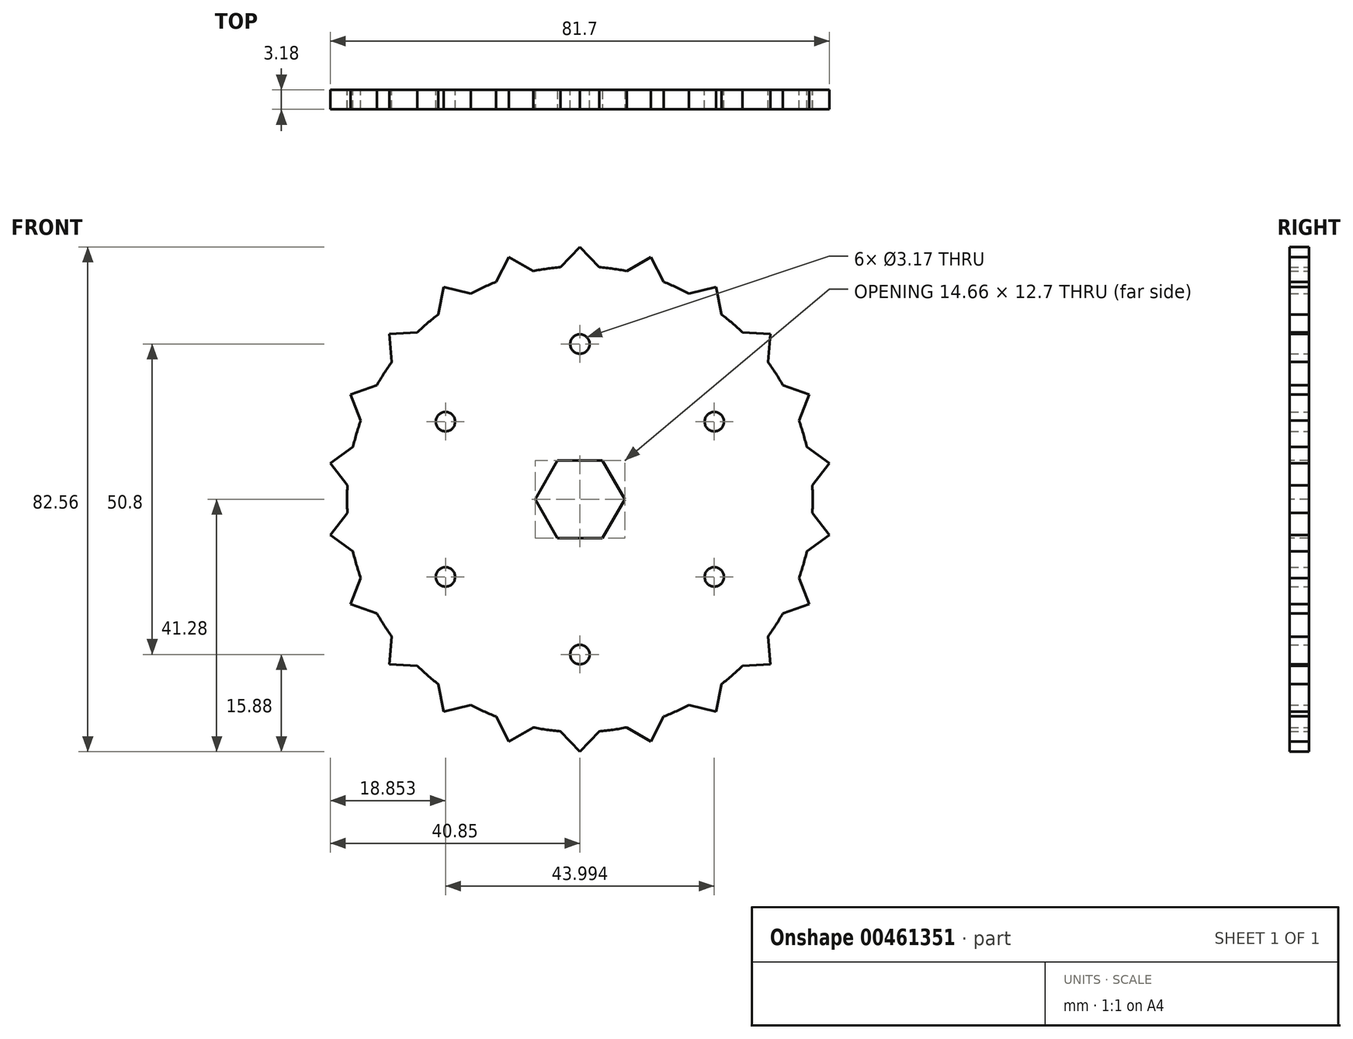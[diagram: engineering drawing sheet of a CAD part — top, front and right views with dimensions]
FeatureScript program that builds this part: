
annotation { "Feature Type Name" : "Feature", "Feature Type Description" : "" }
export const myFeature = defineFeature(function(context is Context, id is Id, definition is map)
    precondition{}
    {
        {
            var Q0;
            Q0=qCreatedBy(makeId("Front.planeOp"),FACE);
            var sketch = newSketch(context, id + "F0", { "sketchPlane" : qUnion([Q0])});
            skArc(sketch, "E0", {"start": v(-23.2, 30.22) * mm, "mid": v(-24.95, 28.8) * mm, "end": v(-26.61, 27.26) * mm});
            skCircle(sketch, "E1", {"center": v(0, 25.4) * mm, "radius": 1.59 * mm});
            skCircle(sketch, "E2.1.0", {"center": v(-22, 12.7) * mm, "radius": 1.59 * mm});
            skCircle(sketch, "E2.2.0", {"center": v(-22, -12.7) * mm, "radius": 1.59 * mm});
            skCircle(sketch, "E2.3.0", {"center": v(0, -25.4) * mm, "radius": 1.59 * mm});
            skCircle(sketch, "E2.4.0", {"center": v(22, -12.7) * mm, "radius": 1.59 * mm});
            skCircle(sketch, "E2.5.0", {"center": v(22, 12.7) * mm, "radius": 1.59 * mm});
            skLineSegment(sketch, "E3", {"start": v(-3.18, 37.97) * mm, "end": v(0, 41.28) * mm});
            skLineSegment(sketch, "E4", {"start": v(0, 41.28) * mm, "end": v(3.18, 37.97) * mm});
            skPoint(sketch, "E5.MirrorCS.end.orphan", {"position": v(3.18, 41.15) * mm});
            skPoint(sketch, "E6.end.orphan", {"position": v(-3.18, 41.15) * mm});
            skLineSegment(sketch, "E7.1.0", {"start": v(-11.63, 39.6) * mm, "end": v(-7.65, 37.32) * mm});
            skLineSegment(sketch, "E7.1.1", {"start": v(-13.74, 35.54) * mm, "end": v(-11.63, 39.6) * mm});
            skLineSegment(sketch, "E7.2.0", {"start": v(-22.31, 34.72) * mm, "end": v(-17.86, 33.66) * mm});
            skLineSegment(sketch, "E7.2.1", {"start": v(-23.2, 30.22) * mm, "end": v(-22.31, 34.72) * mm});
            skLineSegment(sketch, "E7.3.0", {"start": v(-31.2, 27.03) * mm, "end": v(-26.61, 27.26) * mm});
            skLineSegment(sketch, "E7.3.1", {"start": v(-30.77, 22.46) * mm, "end": v(-31.2, 27.03) * mm});
            skLineSegment(sketch, "E7.4.0", {"start": v(-37.55, 17.15) * mm, "end": v(-33.22, 18.66) * mm});
            skLineSegment(sketch, "E7.4.1", {"start": v(-35.86, 12.88) * mm, "end": v(-37.55, 17.15) * mm});
            skLineSegment(sketch, "E7.5.0", {"start": v(-40.85, 5.87) * mm, "end": v(-37.13, 8.55) * mm});
            skLineSegment(sketch, "E7.5.1", {"start": v(-38.03, 2.26) * mm, "end": v(-40.85, 5.87) * mm});
            skLineSegment(sketch, "E7.6.0", {"start": v(-40.85, -5.87) * mm, "end": v(-38.03, -2.26) * mm});
            skLineSegment(sketch, "E7.6.1", {"start": v(-37.13, -8.55) * mm, "end": v(-40.85, -5.87) * mm});
            skLineSegment(sketch, "E7.7.0", {"start": v(-37.55, -17.15) * mm, "end": v(-35.86, -12.88) * mm});
            skLineSegment(sketch, "E7.7.1", {"start": v(-33.22, -18.66) * mm, "end": v(-37.55, -17.15) * mm});
            skLineSegment(sketch, "E7.8.0", {"start": v(-31.2, -27.03) * mm, "end": v(-30.77, -22.46) * mm});
            skLineSegment(sketch, "E7.8.1", {"start": v(-26.61, -27.26) * mm, "end": v(-31.2, -27.03) * mm});
            skLineSegment(sketch, "E7.9.0", {"start": v(-22.31, -34.72) * mm, "end": v(-23.2, -30.22) * mm});
            skLineSegment(sketch, "E7.9.1", {"start": v(-17.86, -33.66) * mm, "end": v(-22.31, -34.72) * mm});
            skLineSegment(sketch, "E7.10.0", {"start": v(-11.63, -39.6) * mm, "end": v(-13.74, -35.54) * mm});
            skLineSegment(sketch, "E7.10.1", {"start": v(-7.65, -37.32) * mm, "end": v(-11.63, -39.6) * mm});
            skLineSegment(sketch, "E7.11.0", {"start": v(0, -41.27) * mm, "end": v(-3.18, -37.97) * mm});
            skLineSegment(sketch, "E7.11.1", {"start": v(3.17, -37.97) * mm, "end": v(0, -41.28) * mm});
            skLineSegment(sketch, "E7.12.0", {"start": v(11.63, -39.6) * mm, "end": v(7.65, -37.32) * mm});
            skLineSegment(sketch, "E7.12.1", {"start": v(13.74, -35.54) * mm, "end": v(11.63, -39.6) * mm});
            skLineSegment(sketch, "E7.13.0", {"start": v(22.31, -34.72) * mm, "end": v(17.86, -33.66) * mm});
            skLineSegment(sketch, "E7.13.1", {"start": v(23.2, -30.22) * mm, "end": v(22.31, -34.72) * mm});
            skLineSegment(sketch, "E7.14.0", {"start": v(31.2, -27.03) * mm, "end": v(26.61, -27.26) * mm});
            skLineSegment(sketch, "E7.14.1", {"start": v(30.77, -22.46) * mm, "end": v(31.2, -27.03) * mm});
            skLineSegment(sketch, "E7.15.0", {"start": v(37.55, -17.15) * mm, "end": v(33.22, -18.66) * mm});
            skLineSegment(sketch, "E7.15.1", {"start": v(35.86, -12.88) * mm, "end": v(37.55, -17.15) * mm});
            skLineSegment(sketch, "E7.16.0", {"start": v(40.85, -5.87) * mm, "end": v(37.13, -8.55) * mm});
            skLineSegment(sketch, "E7.16.1", {"start": v(38.03, -2.26) * mm, "end": v(40.85, -5.87) * mm});
            skLineSegment(sketch, "E7.17.0", {"start": v(40.85, 5.87) * mm, "end": v(38.03, 2.26) * mm});
            skLineSegment(sketch, "E7.17.1", {"start": v(37.13, 8.55) * mm, "end": v(40.85, 5.87) * mm});
            skLineSegment(sketch, "E7.18.0", {"start": v(37.55, 17.15) * mm, "end": v(35.86, 12.88) * mm});
            skLineSegment(sketch, "E7.18.1", {"start": v(33.22, 18.66) * mm, "end": v(37.55, 17.15) * mm});
            skLineSegment(sketch, "E7.19.0", {"start": v(31.2, 27.03) * mm, "end": v(30.77, 22.46) * mm});
            skLineSegment(sketch, "E7.19.1", {"start": v(26.61, 27.26) * mm, "end": v(31.2, 27.03) * mm});
            skLineSegment(sketch, "E7.20.0", {"start": v(22.31, 34.72) * mm, "end": v(23.2, 30.22) * mm});
            skLineSegment(sketch, "E7.20.1", {"start": v(17.86, 33.66) * mm, "end": v(22.31, 34.72) * mm});
            skLineSegment(sketch, "E7.21.0", {"start": v(11.63, 39.6) * mm, "end": v(13.74, 35.54) * mm});
            skLineSegment(sketch, "E7.21.1", {"start": v(7.65, 37.32) * mm, "end": v(11.63, 39.6) * mm});
            skArc(sketch, "E8.trimOffspring", {"start": v(-30.77, 22.46) * mm, "mid": v(-32.05, 20.6) * mm, "end": v(-33.22, 18.66) * mm});
            skArc(sketch, "E9.trimOffspring", {"start": v(-35.86, 12.88) * mm, "mid": v(-36.56, 10.73) * mm, "end": v(-37.13, 8.55) * mm});
            skArc(sketch, "E10.trimOffspring", {"start": v(-38.03, 2.26) * mm, "mid": v(-38.1, 0) * mm, "end": v(-38.03, -2.26) * mm});
            skArc(sketch, "E11.trimOffspring", {"start": v(-37.13, -8.55) * mm, "mid": v(-36.56, -10.73) * mm, "end": v(-35.86, -12.88) * mm});
            skArc(sketch, "E12.trimOffspring", {"start": v(-33.22, -18.66) * mm, "mid": v(-32.05, -20.6) * mm, "end": v(-30.77, -22.46) * mm});
            skArc(sketch, "E13.trimOffspring", {"start": v(-26.61, -27.26) * mm, "mid": v(-24.95, -28.8) * mm, "end": v(-23.2, -30.22) * mm});
            skArc(sketch, "E14.trimOffspring", {"start": v(-17.86, -33.66) * mm, "mid": v(-15.83, -34.66) * mm, "end": v(-13.74, -35.54) * mm});
            skArc(sketch, "E15.trimOffspring", {"start": v(-7.65, -37.32) * mm, "mid": v(-5.42, -37.71) * mm, "end": v(-3.18, -37.97) * mm});
            skArc(sketch, "E16.trimOffspring", {"start": v(3.17, -37.97) * mm, "mid": v(5.42, -37.71) * mm, "end": v(7.65, -37.32) * mm});
            skArc(sketch, "E17.trimOffspring", {"start": v(13.74, -35.54) * mm, "mid": v(15.83, -34.66) * mm, "end": v(17.86, -33.66) * mm});
            skArc(sketch, "E18.trimOffspring", {"start": v(23.2, -30.22) * mm, "mid": v(24.95, -28.8) * mm, "end": v(26.61, -27.26) * mm});
            skArc(sketch, "E19.trimOffspring", {"start": v(30.77, -22.46) * mm, "mid": v(32.05, -20.6) * mm, "end": v(33.22, -18.66) * mm});
            skArc(sketch, "E20.trimOffspring", {"start": v(35.86, -12.88) * mm, "mid": v(36.56, -10.73) * mm, "end": v(37.13, -8.55) * mm});
            skArc(sketch, "E21.trimOffspring", {"start": v(38.03, -2.26) * mm, "mid": v(38.1, 0) * mm, "end": v(38.03, 2.26) * mm});
            skArc(sketch, "E22.trimOffspring", {"start": v(37.13, 8.55) * mm, "mid": v(36.56, 10.73) * mm, "end": v(35.86, 12.88) * mm});
            skArc(sketch, "E23.trimOffspring", {"start": v(33.22, 18.66) * mm, "mid": v(32.05, 20.6) * mm, "end": v(30.77, 22.46) * mm});
            skArc(sketch, "E24.trimOffspring", {"start": v(26.61, 27.26) * mm, "mid": v(24.95, 28.8) * mm, "end": v(23.2, 30.22) * mm});
            skArc(sketch, "E25.trimOffspring", {"start": v(17.86, 33.66) * mm, "mid": v(15.83, 34.66) * mm, "end": v(13.74, 35.54) * mm});
            skArc(sketch, "E26.trimOffspring", {"start": v(7.65, 37.32) * mm, "mid": v(5.42, 37.71) * mm, "end": v(3.18, 37.97) * mm});
            skArc(sketch, "E27.trimOffspring", {"start": v(-3.17, 37.97) * mm, "mid": v(-5.42, 37.71) * mm, "end": v(-7.65, 37.32) * mm});
            skArc(sketch, "E28.trimOffspring", {"start": v(-13.74, 35.54) * mm, "mid": v(-15.83, 34.66) * mm, "end": v(-17.86, 33.66) * mm});
            skSolve(sketch);
        }
        {
            var Q0;
            Q0=makeQuery(id+"F0.imprint","IMPRINT",FACE,{"disambiguationData":[TD([[makeQuery(id+"F0.imprint","IMPRINT",EDGE,{"derivedFrom":sQuery(id+"F0.wireOp",EDGE,"E0")}),1.0]])]});
            extrude(context, id + "F1", {"entities" : qUnion([Q0]), "depth" : 3.17 * mm});
        }
        {
            var Q0;
            Q0=makeQuery(id+"F1.opExtrude","CAP_FACE",FACE,{"disambiguationData":[OSD([sQuery(id+"F0.wireOp",EDGE,"E0"),sQuery(id+"F0.wireOp",EDGE,"E1"),sQuery(id+"F0.wireOp",EDGE,"E2.1.0"),sQuery(id+"F0.wireOp",EDGE,"E2.2.0"),sQuery(id+"F0.wireOp",EDGE,"E2.3.0"),sQuery(id+"F0.wireOp",EDGE,"E2.4.0"),sQuery(id+"F0.wireOp",EDGE,"E2.5.0"),sQuery(id+"F0.wireOp",EDGE,"E3"),sQuery(id+"F0.wireOp",EDGE,"E4"),sQuery(id+"F0.wireOp",EDGE,"E7.1.0"),sQuery(id+"F0.wireOp",EDGE,"E7.1.1"),sQuery(id+"F0.wireOp",EDGE,"E7.2.0"),sQuery(id+"F0.wireOp",EDGE,"E7.2.1"),sQuery(id+"F0.wireOp",EDGE,"E7.3.0"),sQuery(id+"F0.wireOp",EDGE,"E7.3.1"),sQuery(id+"F0.wireOp",EDGE,"E7.4.0"),sQuery(id+"F0.wireOp",EDGE,"E7.4.1"),sQuery(id+"F0.wireOp",EDGE,"E7.5.0"),sQuery(id+"F0.wireOp",EDGE,"E7.5.1"),sQuery(id+"F0.wireOp",EDGE,"E7.6.0"),sQuery(id+"F0.wireOp",EDGE,"E7.6.1"),sQuery(id+"F0.wireOp",EDGE,"E7.7.0"),sQuery(id+"F0.wireOp",EDGE,"E7.7.1"),sQuery(id+"F0.wireOp",EDGE,"E7.8.0"),sQuery(id+"F0.wireOp",EDGE,"E7.8.1"),sQuery(id+"F0.wireOp",EDGE,"E7.9.0"),sQuery(id+"F0.wireOp",EDGE,"E7.9.1"),sQuery(id+"F0.wireOp",EDGE,"E7.10.0"),sQuery(id+"F0.wireOp",EDGE,"E7.10.1"),sQuery(id+"F0.wireOp",EDGE,"E7.11.0"),sQuery(id+"F0.wireOp",EDGE,"E7.11.1"),sQuery(id+"F0.wireOp",EDGE,"E7.12.0"),sQuery(id+"F0.wireOp",EDGE,"E7.12.1"),sQuery(id+"F0.wireOp",EDGE,"E7.13.0"),sQuery(id+"F0.wireOp",EDGE,"E7.13.1"),sQuery(id+"F0.wireOp",EDGE,"E7.14.0"),sQuery(id+"F0.wireOp",EDGE,"E7.14.1"),sQuery(id+"F0.wireOp",EDGE,"E7.15.0"),sQuery(id+"F0.wireOp",EDGE,"E7.15.1"),sQuery(id+"F0.wireOp",EDGE,"E7.16.0"),sQuery(id+"F0.wireOp",EDGE,"E7.16.1"),sQuery(id+"F0.wireOp",EDGE,"E7.17.0"),sQuery(id+"F0.wireOp",EDGE,"E7.17.1"),sQuery(id+"F0.wireOp",EDGE,"E7.18.0"),sQuery(id+"F0.wireOp",EDGE,"E7.18.1"),sQuery(id+"F0.wireOp",EDGE,"E7.19.0"),sQuery(id+"F0.wireOp",EDGE,"E7.19.1"),sQuery(id+"F0.wireOp",EDGE,"E7.20.0"),sQuery(id+"F0.wireOp",EDGE,"E7.20.1"),sQuery(id+"F0.wireOp",EDGE,"E7.21.0"),sQuery(id+"F0.wireOp",EDGE,"E7.21.1"),sQuery(id+"F0.wireOp",EDGE,"E8.trimOffspring"),sQuery(id+"F0.wireOp",EDGE,"E9.trimOffspring"),sQuery(id+"F0.wireOp",EDGE,"E10.trimOffspring"),sQuery(id+"F0.wireOp",EDGE,"E11.trimOffspring"),sQuery(id+"F0.wireOp",EDGE,"E12.trimOffspring"),sQuery(id+"F0.wireOp",EDGE,"E13.trimOffspring"),sQuery(id+"F0.wireOp",EDGE,"E14.trimOffspring"),sQuery(id+"F0.wireOp",EDGE,"E15.trimOffspring"),sQuery(id+"F0.wireOp",EDGE,"E16.trimOffspring"),sQuery(id+"F0.wireOp",EDGE,"E17.trimOffspring"),sQuery(id+"F0.wireOp",EDGE,"E18.trimOffspring"),sQuery(id+"F0.wireOp",EDGE,"E19.trimOffspring"),sQuery(id+"F0.wireOp",EDGE,"E20.trimOffspring"),sQuery(id+"F0.wireOp",EDGE,"E21.trimOffspring"),sQuery(id+"F0.wireOp",EDGE,"E22.trimOffspring"),sQuery(id+"F0.wireOp",EDGE,"E23.trimOffspring"),sQuery(id+"F0.wireOp",EDGE,"E24.trimOffspring"),sQuery(id+"F0.wireOp",EDGE,"E25.trimOffspring"),sQuery(id+"F0.wireOp",EDGE,"E26.trimOffspring"),sQuery(id+"F0.wireOp",EDGE,"E27.trimOffspring"),sQuery(id+"F0.wireOp",EDGE,"E28.trimOffspring")])],"isStart":false});
            var sketch = newSketch(context, id + "F2", { "sketchPlane" : qUnion([Q0])});
            skCircle(sketch, "E29.cCircle", {"center": v(0, 0) * mm, "radius": 6.35 * mm, "construction": true});
            skLineSegment(sketch, "E29.0", {"start": v(-3.67, 6.35) * mm, "end": v(3.67, 6.35) * mm});
            skLineSegment(sketch, "E29.1", {"start": v(3.67, 6.35) * mm, "end": v(7.33, 0) * mm});
            skLineSegment(sketch, "E29.2", {"start": v(7.33, 0) * mm, "end": v(3.67, -6.35) * mm});
            skLineSegment(sketch, "E29.3", {"start": v(3.67, -6.35) * mm, "end": v(-3.67, -6.35) * mm});
            skLineSegment(sketch, "E29.4", {"start": v(-3.67, -6.35) * mm, "end": v(-7.33, 0) * mm});
            skLineSegment(sketch, "E29.5", {"start": v(-7.33, 0) * mm, "end": v(-3.67, 6.35) * mm});
            skPoint(sketch, "E29.0.midPoint", {"position": v(0, 6.35) * mm});
            skSolve(sketch);
        }
        {
            var Q0;
            Q0=makeQuery(id+"F2.imprint","IMPRINT",FACE,{"disambiguationData":[TD([[makeQuery(id+"F2.imprint","IMPRINT",EDGE,{"derivedFrom":sQuery(id+"F2.wireOp",EDGE,"E29.0")}),-1.0]])]});
            extrude(context, id + "F3", {"entities" : qUnion([Q0]), "operationType" : NewBodyOperationType.REMOVE, "endBound" : BoundingType.THROUGH_ALL, "oppositeDirection" : true, "depth" : 25.4 * mm});
        }
    });
